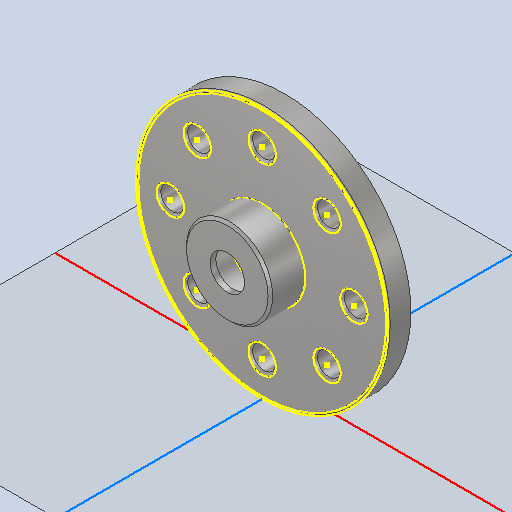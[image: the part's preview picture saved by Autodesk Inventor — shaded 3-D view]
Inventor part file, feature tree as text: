
AUTODESK INVENTOR PART (.ipt)
format: ipt  version: 2022 (Build 260153000, 153)  size: 193,024 bytes
history: mixed  units: mm
features: chamfer x2, sketch x1, projected_geometry x1, imported_body x1
ambient origin geometry x8: Origin, YZ Plane, XZ Plane, XY Plane, X Axis, Y Axis, Z Axis, Center Point
bodies: Solid1 (imported_parasolid), Solid2 (imported_parasolid)
feature tree (5):
  sketch  "Эскиз1"
  projected_geometry  "Спроецированная петля1"
  chamfer  "Chamfer2"  [1 undecoded]
  chamfer  "Chamfer5"  [1 undecoded]
  imported_body  NMx_Import_Brep_tag  [imported B-rep: ~28 faces, bbox_mm=[19.0, 16.0, 5.0]]
note: 2 required parameter values undecoded (feature->parameter linkage not recoverable at this tier; creation-order binding heuristic only, values carry confidence <= 0.55)
